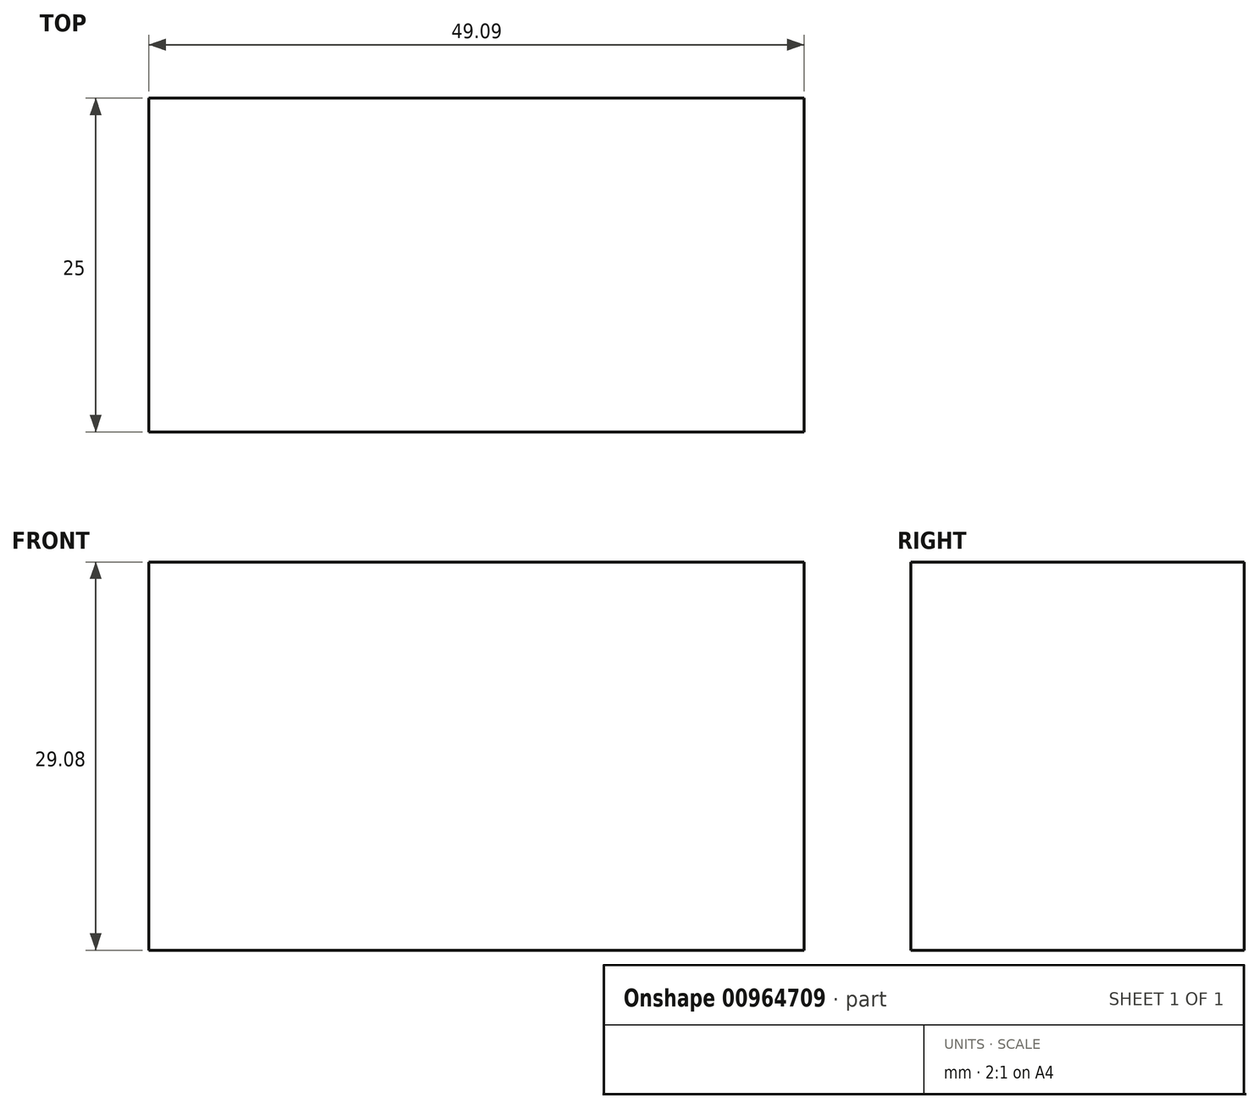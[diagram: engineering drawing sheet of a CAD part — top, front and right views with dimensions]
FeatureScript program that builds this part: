
annotation { "Feature Type Name" : "Feature", "Feature Type Description" : "" }
export const myFeature = defineFeature(function(context is Context, id is Id, definition is map)
    precondition{}
    {
        {
            var Q0;
            Q0=qCreatedBy(makeId("Front.planeOp"),FACE);
            var sketch = newSketch(context, id + "F0", { "sketchPlane" : qUnion([Q0])});
            skLineSegment(sketch, "E0.bottom", {"start": v(-101.55, 56.46) * mm, "end": v(-52.46, 56.46) * mm});
            skLineSegment(sketch, "E0.top", {"start": v(-101.55, 27.38) * mm, "end": v(-52.46, 27.38) * mm});
            skLineSegment(sketch, "E0.left", {"start": v(-101.55, 56.46) * mm, "end": v(-101.55, 27.38) * mm});
            skLineSegment(sketch, "E0.right", {"start": v(-52.46, 56.46) * mm, "end": v(-52.46, 27.38) * mm});
            skSolve(sketch);
        }
        {
            var Q0;
            Q0 = qSketchRegion(id + "F0", true);
            extrude(context, id + "F1", {"entities" : qUnion([Q0]), "depth" : 25 * mm, "offsetDistance" : 25 * mm});
        }
    });
